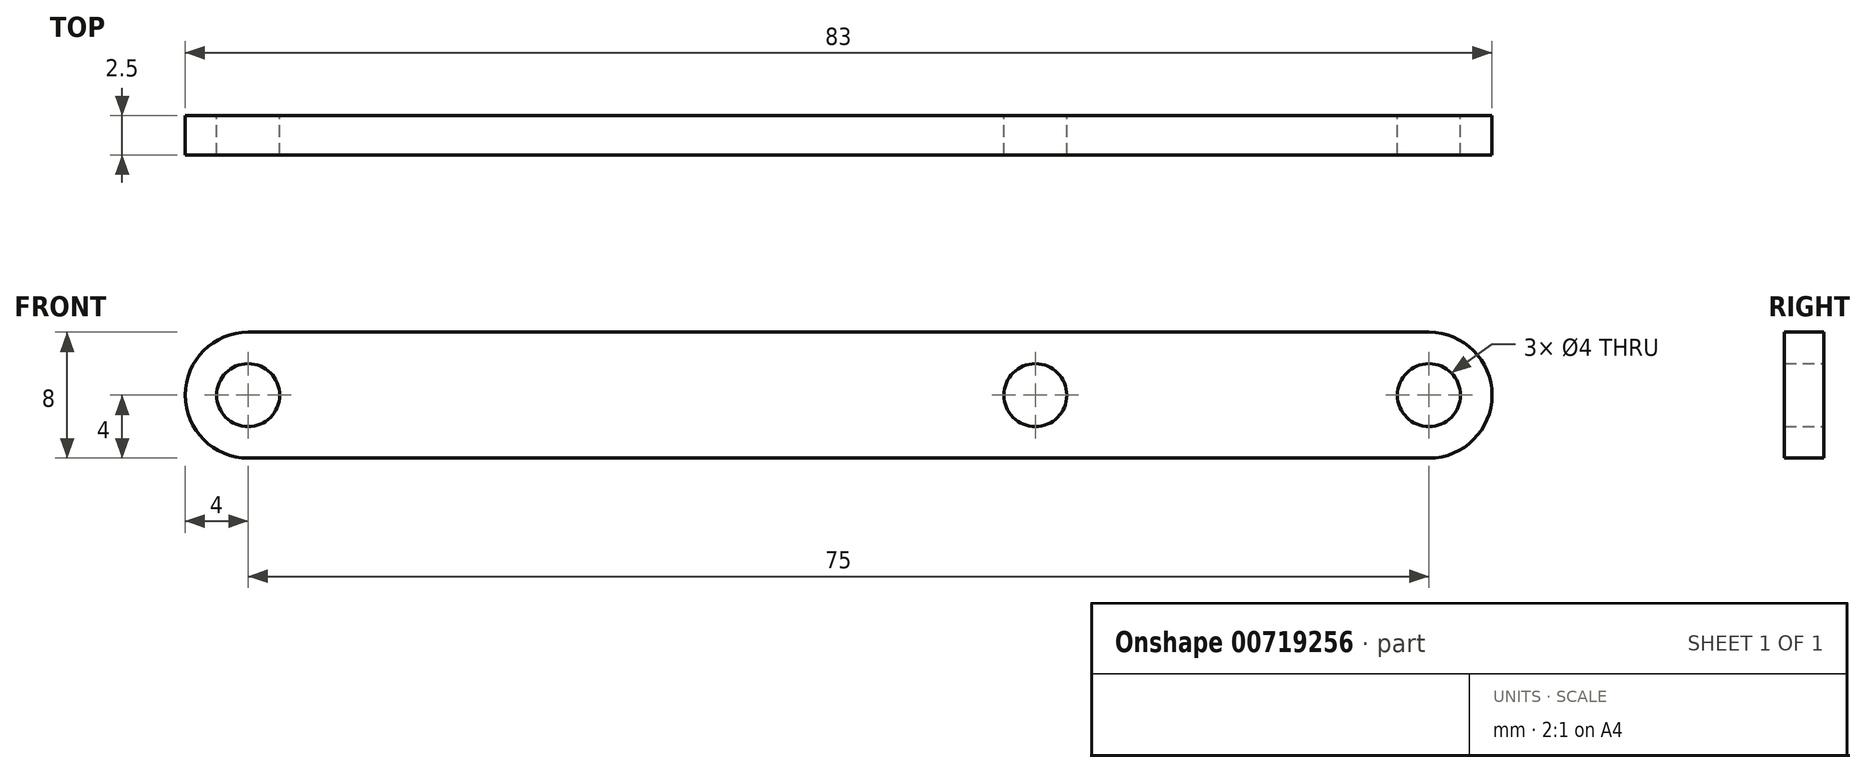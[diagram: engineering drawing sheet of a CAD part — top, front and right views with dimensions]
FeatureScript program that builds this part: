
annotation { "Feature Type Name" : "Feature", "Feature Type Description" : "" }
export const myFeature = defineFeature(function(context is Context, id is Id, definition is map)
    precondition{}
    {
        {
            var Q0;
            Q0=qCreatedBy(makeId("Front.planeOp"),FACE);
            var sketch = newSketch(context, id + "F0", { "sketchPlane" : qUnion([Q0])});
            skArc(sketch, "E0", {"start": v(0, -4) * mm, "mid": v(4, 0) * mm, "end": v(0, 4) * mm});
            skArc(sketch, "E1", {"start": v(-75, 4) * mm, "mid": v(-79, 0) * mm, "end": v(-75, -4) * mm});
            skLineSegment(sketch, "E2", {"start": v(0, 4) * mm, "end": v(-75, 4) * mm});
            skLineSegment(sketch, "E3", {"start": v(0, -4) * mm, "end": v(-75, -4) * mm});
            skCircle(sketch, "E4", {"center": v(0, 0) * mm, "radius": 2 * mm});
            skCircle(sketch, "E5", {"center": v(-75, 0) * mm, "radius": 2 * mm});
            skCircle(sketch, "E6", {"center": v(-25, 0) * mm, "radius": 2 * mm});
            skSolve(sketch);
        }
        {
            var Q0;
            Q0 = qSketchRegion(id + "F0", true);
            extrude(context, id + "F1", {"entities" : qUnion([Q0]), "depth" : 2.5 * mm, "offsetDistance" : 25.4 * mm});
        }
    });
